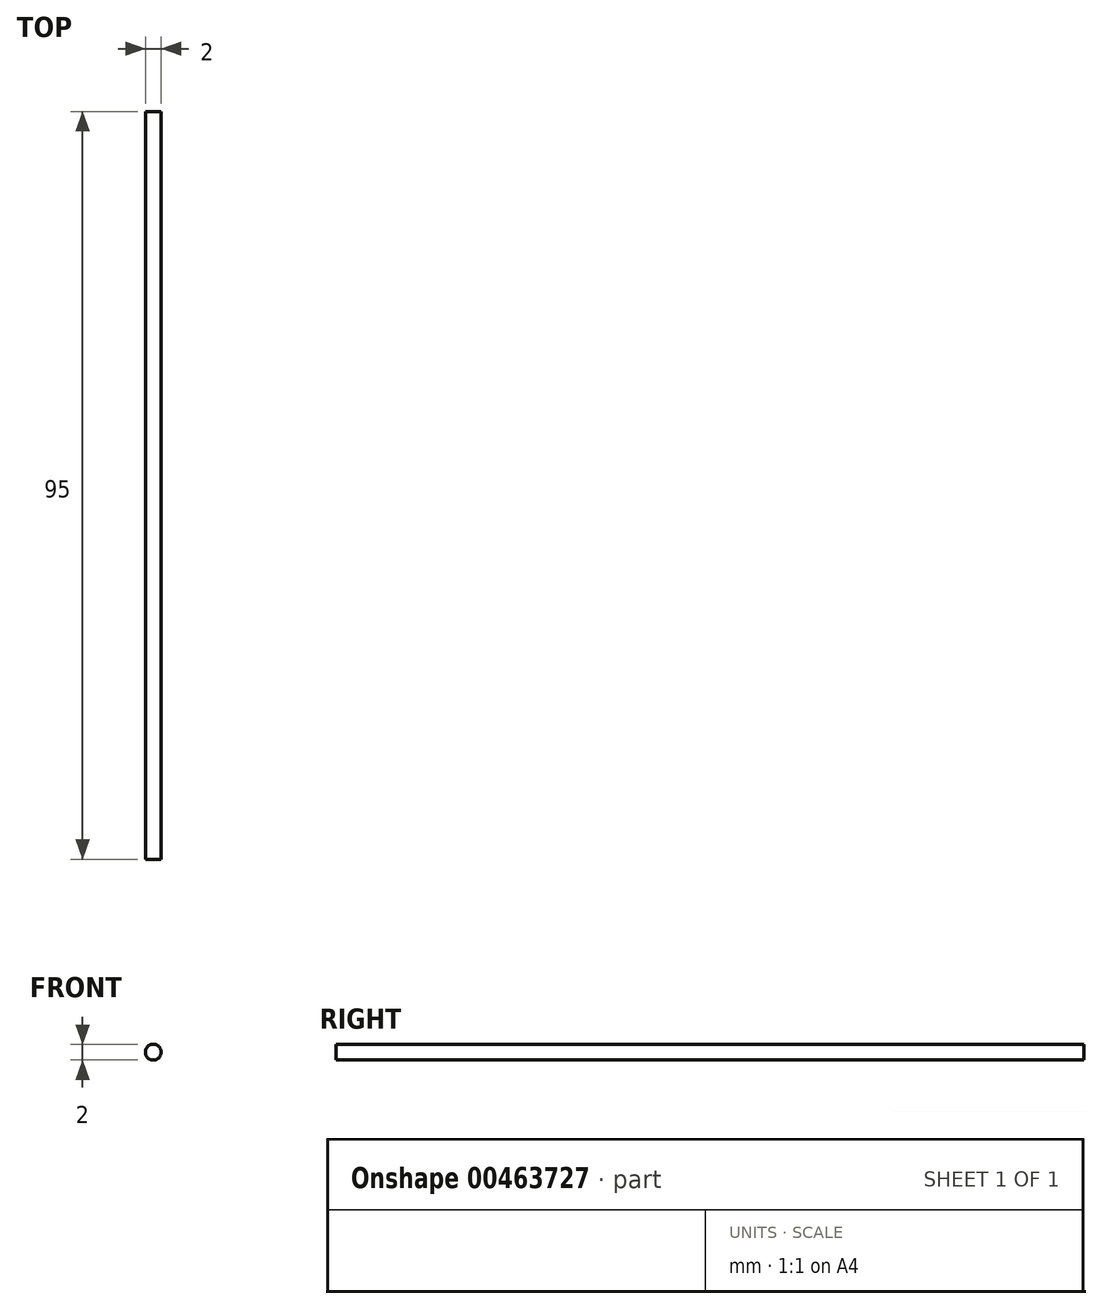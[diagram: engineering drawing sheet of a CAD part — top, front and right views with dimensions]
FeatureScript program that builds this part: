
annotation { "Feature Type Name" : "Feature", "Feature Type Description" : "" }
export const myFeature = defineFeature(function(context is Context, id is Id, definition is map)
    precondition{}
    {
        {
            var Q0;
            Q0=qCreatedBy(makeId("Front.planeOp"),FACE);
            var sketch = newSketch(context, id + "F0", { "sketchPlane" : qUnion([Q0])});
            skCircle(sketch, "E0", {"center": v(-24.2, -7.12) * mm, "radius": 1 * mm});
            skSolve(sketch);
        }
        {
            var Q0;
            Q0=makeQuery(id+"F0.imprint","IMPRINT",FACE,{"disambiguationData":[TD([[makeQuery(id+"F0.imprint","IMPRINT",EDGE,{"derivedFrom":sQuery(id+"F0.wireOp",EDGE,"E0")}),1.0]])]});
            extrude(context, id + "F1", {"entities" : qUnion([Q0]), "endBound" : BoundingType.SYMMETRIC, "depth" : 95 * mm});
        }
    });
